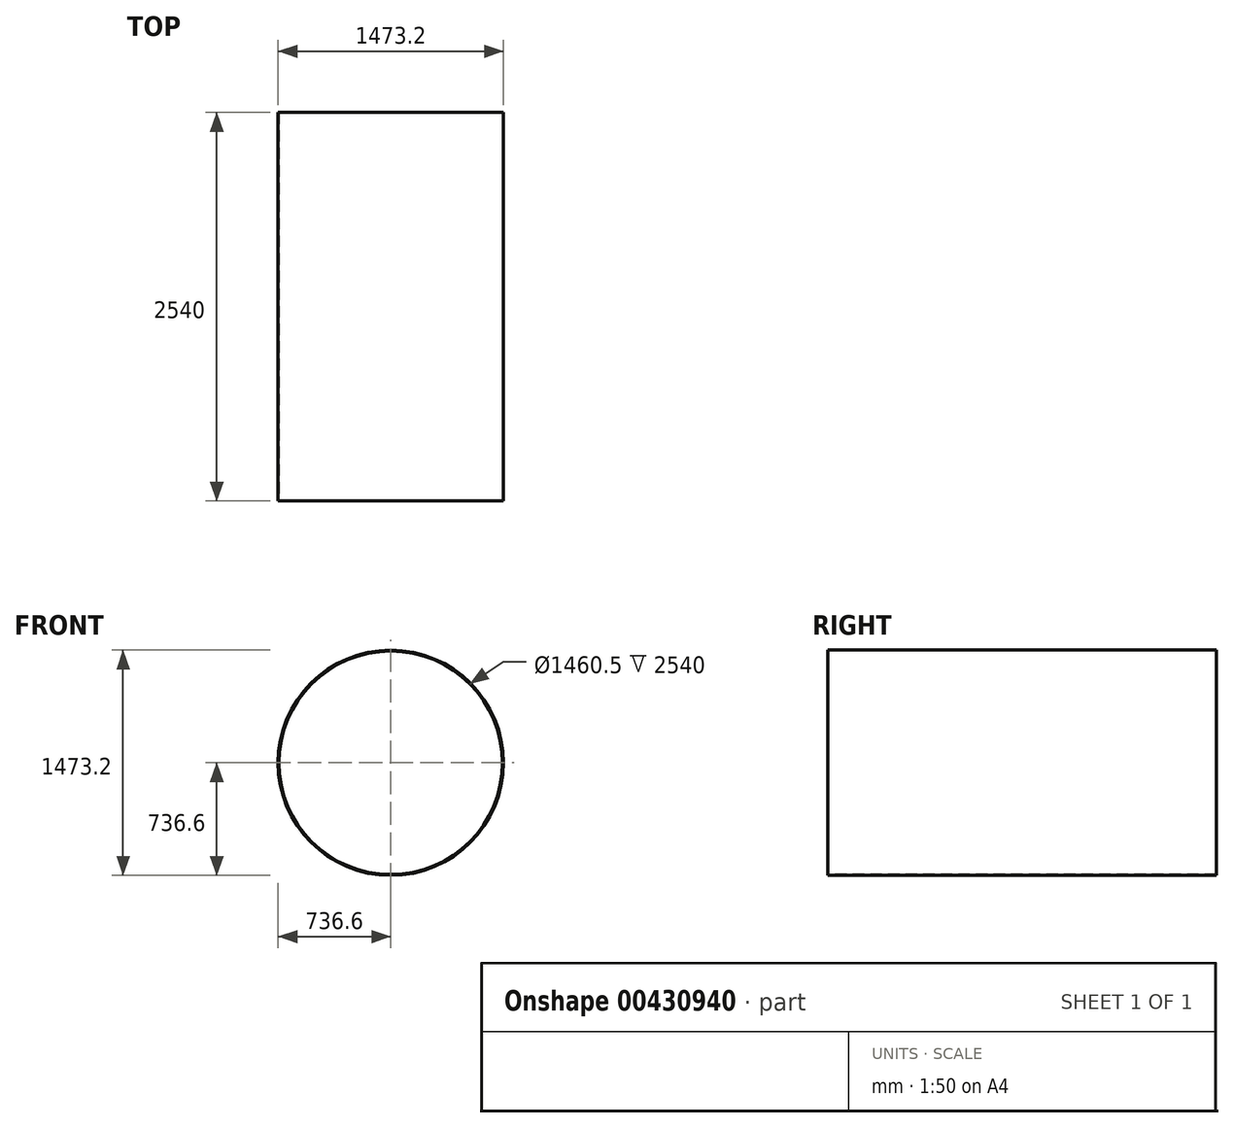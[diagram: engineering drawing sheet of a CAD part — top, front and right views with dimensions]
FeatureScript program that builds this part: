
annotation { "Feature Type Name" : "Feature", "Feature Type Description" : "" }
export const myFeature = defineFeature(function(context is Context, id is Id, definition is map)
    precondition{}
    {
        {
            var Q0;
            Q0=qCreatedBy(makeId("Front.planeOp"),FACE);
            var sketch = newSketch(context, id + "F0", { "sketchPlane" : qUnion([Q0])});
            skCircle(sketch, "E0", {"center": v(0, 0) * mm, "radius": 736.6 * mm});
            skCircle(sketch, "E1", {"center": v(0, 0) * mm, "radius": 730.25 * mm});
            skSolve(sketch);
        }
        {
            var Q0;
            Q0=makeQuery(id+"F0.imprint","IMPRINT",FACE,{"disambiguationData":[TD([[makeQuery(id+"F0.imprint","IMPRINT",EDGE,{"derivedFrom":sQuery(id+"F0.wireOp",EDGE,"E0")}),1.0]])]});
            extrude(context, id + "F1", {"entities" : qUnion([Q0]), "oppositeDirection" : true, "depth" : 2540 * mm});
        }
    });
